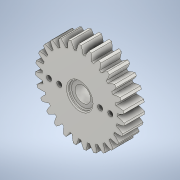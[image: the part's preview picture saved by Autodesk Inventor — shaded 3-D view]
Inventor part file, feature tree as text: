
AUTODESK INVENTOR PART (.ipt)
format: ipt  version: 2022 (Build 260153000, 153)  size: 521,728 bytes
history: native  units: mm (DEFAULTED — no unit token found)
features: sketch x6, extrude x5, plane x3, other x3, fillet x1, projected_geometry x1
ambient origin geometry x8: Origin, YZ Plane, XZ Plane, XY Plane, X Axis, Y Axis, Z Axis, Center Point
bodies: Solid1 (feature_tree)
feature tree (19):
  extrude  "Extrusion1"  Depth=6.0mm TaperAngle=0.0deg
  plane  "Work Plane2"
  plane  "Work Plane8"
  plane  "Work Plane9"
  other  "Цилиндрическое зубчатое зацепление"
  extrude  "Выдавливание5"  Depth=10.0mm TaperAngle=0.0deg
  extrude  "Выдавливание3"  Depth=0.5mm
  extrude  "Выдавливание4"  Depth=0.5mm TaperAngle=0.0deg
  extrude  "Выдавливание6"  TaperAngle=0.0deg  [1 undecoded]
  fillet  "Сопряжение1"  [1 undecoded]
  sketch  "Sketch1"  dims[d0=43.480844mm d1=6.0mm d2=0.0mm]
  sketch  "Sketch2"  dims[d3=40.5mm d4=10.0mm d5=0.0mm d16=40.825mm d17=0.0mm d34=1.163553mm d39=0.0mm d41=0.0mm d43=40.825mm d46=40.825mm d47=0.0mm d48=0.0mm d52=7.6mm d53=10.0mm d54=2.5mm d55=5.0mm d56=20.0mm d58=360.0deg d60=100.0mm d61=0.0mm d62=5.2mm d67=1.5mm d68=0.0mm d69=5.2mm d70=20.0mm d72=360.0deg d74=4.0mm d75=0.0mm d76=12.0mm d77=1.5mm d78=0.0mm d79=0.5mm]
  other  "Srf1"
  sketch  "Эскиз4"
  sketch  "Эскиз5"
  sketch  "Эскиз6"
  projected_geometry  "Спроецированная петля1"
  sketch  "Эскиз7"
  other  "Средний диаметр"
note: 2 required parameter values undecoded (feature->parameter linkage not recoverable at this tier; creation-order binding heuristic only, values carry confidence <= 0.55)
